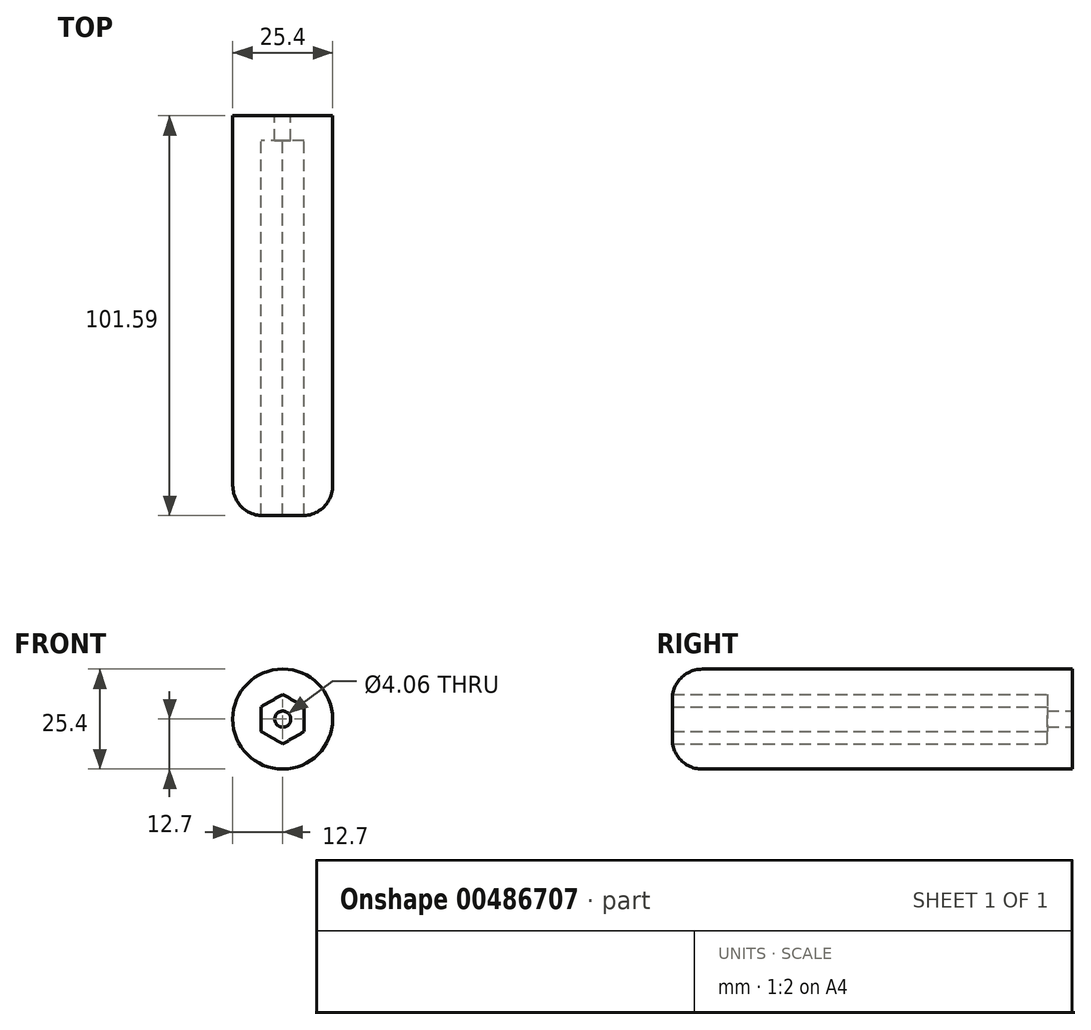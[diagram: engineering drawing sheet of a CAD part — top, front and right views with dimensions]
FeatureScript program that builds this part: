
annotation { "Feature Type Name" : "Feature", "Feature Type Description" : "" }
export const myFeature = defineFeature(function(context is Context, id is Id, definition is map)
    precondition{}
    {
        {
            var Q0;
            Q0=qCreatedBy(makeId("Front.planeOp"),FACE);
            var sketch = newSketch(context, id + "F0", { "sketchPlane" : qUnion([Q0])});
            skCircle(sketch, "E0", {"center": v(0, 0) * mm, "radius": 12.7 * mm});
            skCircle(sketch, "E1.cCircle", {"center": v(0, 0) * mm, "radius": 6.3 * mm, "construction": true});
            skLineSegment(sketch, "E1.0", {"start": v(0, -6.3) * mm, "end": v(-5.45, -3.15) * mm});
            skLineSegment(sketch, "E1.1", {"start": v(-5.45, -3.15) * mm, "end": v(-5.45, 3.15) * mm});
            skLineSegment(sketch, "E1.2", {"start": v(-5.45, 3.15) * mm, "end": v(0, 6.3) * mm});
            skLineSegment(sketch, "E1.3", {"start": v(0, 6.3) * mm, "end": v(5.45, 3.15) * mm});
            skLineSegment(sketch, "E1.4", {"start": v(5.45, 3.15) * mm, "end": v(5.45, -3.15) * mm});
            skLineSegment(sketch, "E1.5", {"start": v(5.45, -3.15) * mm, "end": v(0, -6.3) * mm});
            skCircle(sketch, "E2", {"center": v(0, 0) * mm, "radius": 2.03 * mm});
            skSolve(sketch);
        }
        {
            var Q0;
            Q0=makeQuery(id+"F0.imprint","IMPRINT",FACE,{"disambiguationData":[TD([[makeQuery(id+"F0.imprint","IMPRINT",EDGE,{"derivedFrom":sQuery(id+"F0.wireOp",EDGE,"E1.0")}),-1.0]])]});
            extrude(context, id + "F1", {"entities" : qUnion([Q0]), "depth" : 6.35 * mm});
        }
        {
            var Q0;
            Q0=makeQuery(id+"F0.imprint","IMPRINT",FACE,{"disambiguationData":[TD([[makeQuery(id+"F0.imprint","IMPRINT",EDGE,{"derivedFrom":sQuery(id+"F0.wireOp",EDGE,"E0")}),1.0]])]});
            extrude(context, id + "F2", {"entities" : qUnion([Q0]), "operationType" : NewBodyOperationType.ADD, "depth" : 101.6 * mm});
        }
        {
            var Q0;
            Q0=makeQuery(id+"F2.opExtrude","CAP_EDGE",EDGE,{"disambiguationData":[OSD([sQuery(id+"F0.wireOp",EDGE,"E0")])],"isStart":false});
            fillet(context, id + "F3", {"entities" : qUnion([Q0]), "radius" : 7.62 * mm, "tangentPropagation" : true, "allowEdgeOverflow" : false});
        }
        {
            var Q0;
            Q0=qCreatedBy(makeId("Right.planeOp"),FACE);
            var sketch = newSketch(context, id + "F4", { "sketchPlane" : qUnion([Q0])});
            skLineSegment(sketch, "E3", {"start": v(-93.4, 11.67) * mm, "end": v(-84.59, 20) * mm});
            skLineSegment(sketch, "E4", {"start": v(-75.6, 19.75) * mm, "end": v(-72.86, 16.85) * mm});
            skLineSegment(sketch, "E5", {"start": v(-63.89, 16.6) * mm, "end": v(-60.75, 19.57) * mm});
            skLineSegment(sketch, "E6", {"start": v(-51.77, 19.32) * mm, "end": v(-49.48, 16.9) * mm});
            skLineSegment(sketch, "E7", {"start": v(-40.5, 16.65) * mm, "end": v(-37.95, 19.07) * mm});
            skLineSegment(sketch, "E8", {"start": v(-28.97, 18.82) * mm, "end": v(-27.01, 16.74) * mm});
            skLineSegment(sketch, "E9", {"start": v(-18.04, 16.5) * mm, "end": v(-17, 17.47) * mm});
            skLineSegment(sketch, "E10", {"start": v(-8.02, 17.23) * mm, "end": v(-3.26, 12.19) * mm});
            skPoint(sketch, "E11.visualSharp", {"position": v(-79.97, 24.36) * mm});
            skArc(sketch, "E11.filletArc", {"start": v(-75.6, 19.75) * mm, "mid": v(-80.05, 21.74) * mm, "end": v(-84.59, 20) * mm});
            skPoint(sketch, "E12.visualSharp", {"position": v(-56.14, 23.93) * mm});
            skArc(sketch, "E12.filletArc", {"start": v(-51.77, 19.32) * mm, "mid": v(-56.2, 21.3) * mm, "end": v(-60.75, 19.57) * mm});
            skPoint(sketch, "E13.visualSharp", {"position": v(-12.39, 21.84) * mm});
            skArc(sketch, "E13.filletArc", {"start": v(-8.02, 17.23) * mm, "mid": v(-12.46, 19.2) * mm, "end": v(-17, 17.47) * mm});
            skPoint(sketch, "E14.visualSharp", {"position": v(-33.34, 23.43) * mm});
            skArc(sketch, "E14.filletArc", {"start": v(-28.97, 18.82) * mm, "mid": v(-33.41, 20.8) * mm, "end": v(-37.95, 19.07) * mm});
            skPoint(sketch, "E15.visualSharp", {"position": v(-68.5, 12.24) * mm});
            skArc(sketch, "E15.filletArc", {"start": v(-72.86, 16.85) * mm, "mid": v(-68.43, 14.86) * mm, "end": v(-63.89, 16.6) * mm});
            skPoint(sketch, "E16.visualSharp", {"position": v(-45.12, 12.29) * mm});
            skArc(sketch, "E16.filletArc", {"start": v(-49.48, 16.9) * mm, "mid": v(-45.05, 14.91) * mm, "end": v(-40.5, 16.65) * mm});
            skPoint(sketch, "E17.visualSharp", {"position": v(-22.65, 12.13) * mm});
            skArc(sketch, "E17.filletArc", {"start": v(-27.01, 16.74) * mm, "mid": v(-22.58, 14.76) * mm, "end": v(-18.04, 16.5) * mm});
            skSolve(sketch);
        }
        {
            var Q0;
            Q0=sQuery(id+"F4.wireOp",EDGE,"E4");
            var Q1;
            Q1=sQuery(id+"F4.wireOp",EDGE,"E11.filletArc");
            var Q2;
            Q2=sQuery(id+"F4.wireOp",EDGE,"E3");
            var Q3;
            Q3=sQuery(id+"F4.wireOp",EDGE,"E15.filletArc");
            var Q4;
            Q4=sQuery(id+"F4.wireOp",EDGE,"E12.filletArc");
            var Q5;
            Q5=sQuery(id+"F4.wireOp",EDGE,"E5");
            var Q6;
            Q6=sQuery(id+"F4.wireOp",EDGE,"E6");
            var Q7;
            Q7=sQuery(id+"F4.wireOp",EDGE,"E16.filletArc");
            var Q8;
            Q8=sQuery(id+"F4.wireOp",EDGE,"E7");
            var Q9;
            Q9=sQuery(id+"F4.wireOp",EDGE,"E14.filletArc");
            var Q10;
            Q10=sQuery(id+"F4.wireOp",EDGE,"E17.filletArc");
            var Q11;
            Q11=sQuery(id+"F4.wireOp",EDGE,"E8");
            var Q12;
            Q12=sQuery(id+"F4.wireOp",EDGE,"E9");
            var Q13;
            Q13=sQuery(id+"F4.wireOp",EDGE,"E13.filletArc");
            var Q14;
            Q14=sQuery(id+"F4.wireOp",EDGE,"E10");
            var Q15;
            Q15=makeQuery(id+"F2.opExtrude","SWEPT_FACE",FACE,{"disambiguationData":[OSD([sQuery(id+"F0.wireOp",EDGE,"E0")])]});
            revolve(context, id + "F5", {"bodyType" : ToolBodyType.SURFACE, "operationType" : NewBodyOperationType.ADD, "surfaceEntities" : qUnion([Q0, Q1, Q2, Q3, Q4, Q5, Q6, Q7, Q8, Q9, Q10, Q11, Q12, Q13, Q14]), "axis" : qUnion([Q15]), "revolveType" : RevolveType.FULL});
        }
    });
